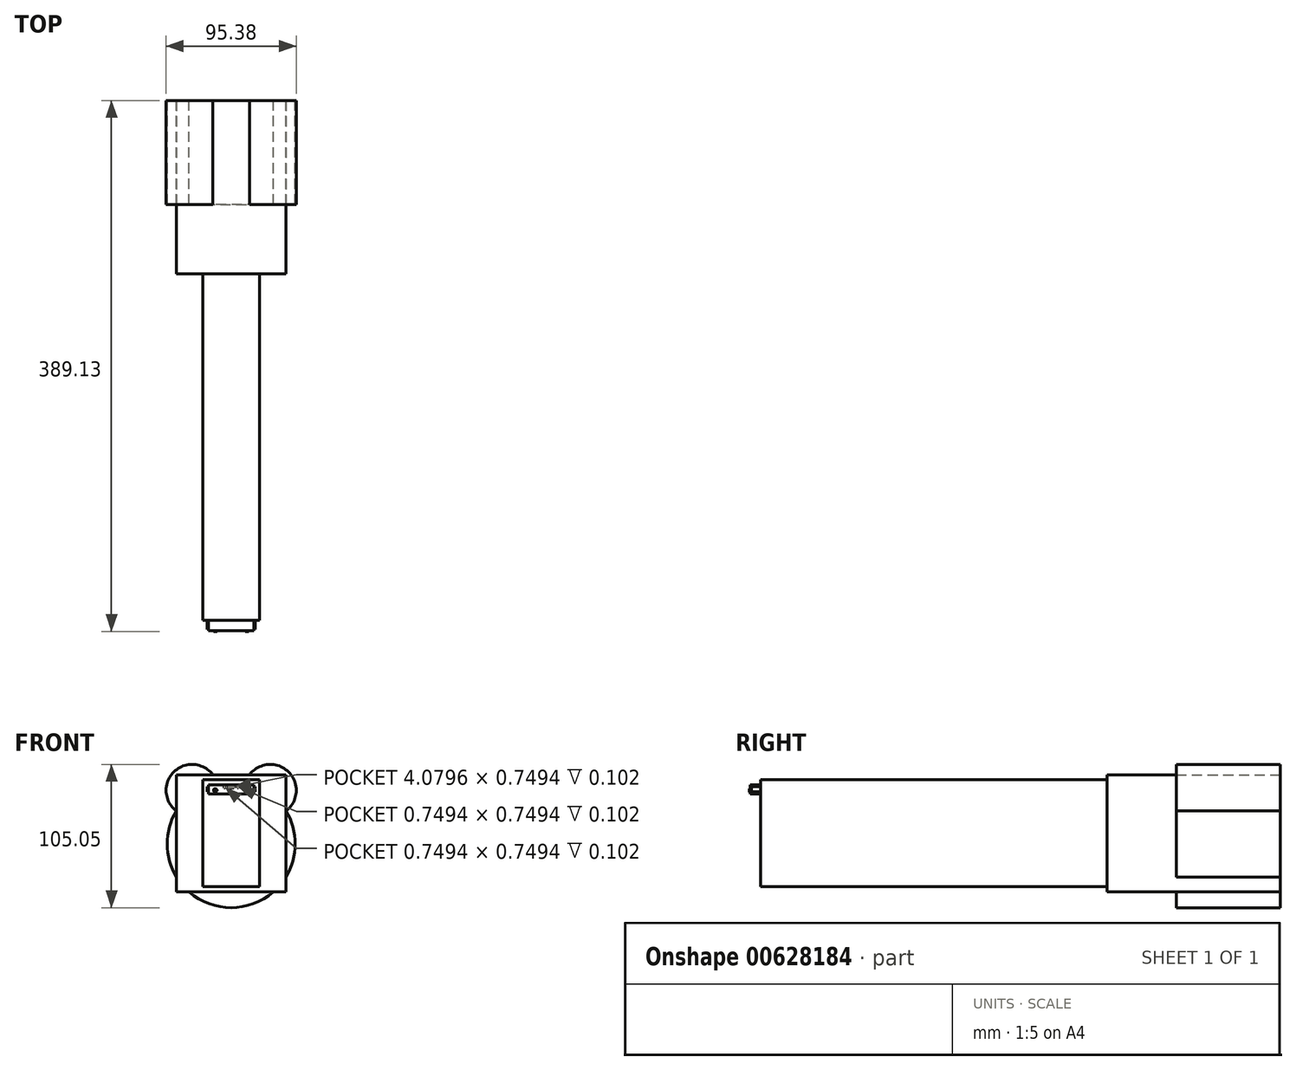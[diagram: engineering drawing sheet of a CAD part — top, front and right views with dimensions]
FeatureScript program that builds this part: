
annotation { "Feature Type Name" : "Feature", "Feature Type Description" : "" }
export const myFeature = defineFeature(function(context is Context, id is Id, definition is map)
    precondition{}
    {
        {
            var Q0;
            Q0=qCreatedBy(makeId("Front.planeOp"),FACE);
            var sketch = newSketch(context, id + "F0", { "sketchPlane" : qUnion([Q0])});
            skLineSegment(sketch, "E0.bottom", {"start": v(20.72, 39.2) * mm, "end": v(-20.72, 39.2) * mm});
            skLineSegment(sketch, "E0.top", {"start": v(20.72, -39.2) * mm, "end": v(-20.72, -39.2) * mm});
            skLineSegment(sketch, "E0.left", {"start": v(20.72, 39.2) * mm, "end": v(20.72, -39.2) * mm});
            skLineSegment(sketch, "E0.right", {"start": v(-20.72, 39.2) * mm, "end": v(-20.72, -39.2) * mm});
            skPoint(sketch, "E0.middle", {"position": v(0, 0) * mm});
            skSolve(sketch);
        }
        {
            var Q0;
            Q0 = qSketchRegion(id + "F0", true);
            extrude(context, id + "F1", {"entities" : qUnion([Q0]), "depth" : 254 * mm, "offsetDistance" : 25.4 * mm});
        }
        {
            var Q0;
            Q0=qCreatedBy(makeId("Front.planeOp"),FACE);
            var sketch = newSketch(context, id + "F2", { "sketchPlane" : qUnion([Q0])});
            skLineSegment(sketch, "E1.bottom", {"start": v(-40.07, 42.92) * mm, "end": v(40.07, 42.92) * mm});
            skLineSegment(sketch, "E1.top", {"start": v(-40.07, -42.92) * mm, "end": v(40.07, -42.92) * mm});
            skLineSegment(sketch, "E1.left", {"start": v(-40.07, 42.92) * mm, "end": v(-40.07, -42.92) * mm});
            skLineSegment(sketch, "E1.right", {"start": v(40.07, 42.92) * mm, "end": v(40.07, -42.92) * mm});
            skPoint(sketch, "E1.middle", {"position": v(0, 0) * mm});
            skSolve(sketch);
        }
        {
            var Q0;
            Q0=makeQuery(id+"F2.imprint","IMPRINT",FACE,{"disambiguationData":[TD([[makeQuery(id+"F2.imprint","IMPRINT",EDGE,{"derivedFrom":sQuery(id+"F2.wireOp",EDGE,"E1.bottom")}),-1.0]])]});
            extrude(context, id + "F3", {"entities" : qUnion([Q0]), "operationType" : NewBodyOperationType.ADD, "oppositeDirection" : true, "depth" : 127 * mm, "offsetDistance" : 25.4 * mm});
        }
        {
            var Q0;
            Q0=makeQuery(id+"F1.opExtrude","CAP_FACE",FACE,{"disambiguationData":[OSD([sQuery(id+"F0.wireOp",EDGE,"E0.bottom"),sQuery(id+"F0.wireOp",EDGE,"E0.top"),sQuery(id+"F0.wireOp",EDGE,"E0.left"),sQuery(id+"F0.wireOp",EDGE,"E0.right")])],"isStart":false});
            var sketch = newSketch(context, id + "F4", { "sketchPlane" : qUnion([Q0])});
            skLineSegment(sketch, "E2.bottom", {"start": v(16.75, 29.03) * mm, "end": v(-16.75, 29.03) * mm});
            skLineSegment(sketch, "E2.top", {"start": v(16.75, 35.48) * mm, "end": v(-16.75, 35.48) * mm});
            skLineSegment(sketch, "E2.left", {"start": v(16.75, 29.03) * mm, "end": v(16.75, 35.48) * mm});
            skLineSegment(sketch, "E2.right", {"start": v(-16.75, 29.03) * mm, "end": v(-16.75, 35.48) * mm});
            skPoint(sketch, "E2.middle", {"position": v(0, 32.25) * mm});
            skSolve(sketch);
        }
        {
            var Q0;
            Q0 = qSketchRegion(id + "F4", true);
            extrude(context, id + "F5", {"entities" : qUnion([Q0]), "operationType" : NewBodyOperationType.ADD, "depth" : 7.62 * mm, "offsetDistance" : 25.4 * mm});
        }
        {
            var Q0;
            Q0=makeQuery(id+"F5.opExtrude","CAP_FACE",FACE,{"disambiguationData":[OSD([sQuery(id+"F4.wireOp",EDGE,"E2.bottom"),sQuery(id+"F4.wireOp",EDGE,"E2.top"),sQuery(id+"F4.wireOp",EDGE,"E2.left"),sQuery(id+"F4.wireOp",EDGE,"E2.right")])],"isStart":false});
            var sketch = newSketch(context, id + "F6", { "sketchPlane" : qUnion([Q0])});
            skLineSegment(sketch, "E3.bottom", {"start": v(2.04, 33.46) * mm, "end": v(-2.04, 33.46) * mm});
            skLineSegment(sketch, "E3.top", {"start": v(2.04, 34.2) * mm, "end": v(-2.04, 34.2) * mm});
            skLineSegment(sketch, "E3.left", {"start": v(2.04, 33.46) * mm, "end": v(2.04, 34.2) * mm});
            skLineSegment(sketch, "E3.right", {"start": v(-2.04, 33.46) * mm, "end": v(-2.04, 34.2) * mm});
            skPoint(sketch, "E3.middle", {"position": v(0, 33.83) * mm});
            skLineSegment(sketch, "E4.bottom", {"start": v(4.58, 34.2) * mm, "end": v(5.33, 34.2) * mm});
            skLineSegment(sketch, "E4.top", {"start": v(4.58, 33.46) * mm, "end": v(5.33, 33.46) * mm});
            skLineSegment(sketch, "E4.left", {"start": v(4.58, 34.2) * mm, "end": v(4.58, 33.46) * mm});
            skLineSegment(sketch, "E4.right", {"start": v(5.33, 34.2) * mm, "end": v(5.33, 33.46) * mm});
            skLineSegment(sketch, "E5.bottom", {"start": v(-4.58, 34.2) * mm, "end": v(-5.33, 34.2) * mm});
            skLineSegment(sketch, "E5.top", {"start": v(-4.58, 33.46) * mm, "end": v(-5.33, 33.46) * mm});
            skLineSegment(sketch, "E5.left", {"start": v(-4.58, 34.2) * mm, "end": v(-4.58, 33.46) * mm});
            skLineSegment(sketch, "E5.right", {"start": v(-5.33, 34.2) * mm, "end": v(-5.33, 33.46) * mm});
            skSolve(sketch);
        }
        {
            var Q0;
            Q0 = qSketchRegion(id + "F6", true);
            extrude(context, id + "F7", {"entities" : qUnion([Q0]), "operationType" : NewBodyOperationType.REMOVE, "oppositeDirection" : true, "depth" : 0.1 * mm, "offsetDistance" : 25.4 * mm});
        }
        {
            var Q0;
            Q0=makeQuery(id+"F5.opExtrude","CAP_FACE",FACE,{"disambiguationData":[OSD([sQuery(id+"F4.wireOp",EDGE,"E2.bottom"),sQuery(id+"F4.wireOp",EDGE,"E2.top"),sQuery(id+"F4.wireOp",EDGE,"E2.left"),sQuery(id+"F4.wireOp",EDGE,"E2.right")])],"isStart":false});
            var sketch = newSketch(context, id + "F8", { "sketchPlane" : qUnion([Q0])});
            skCircle(sketch, "E6", {"center": v(-11.67, 31.57) * mm, "radius": 1.27 * mm});
            skCircle(sketch, "E7", {"center": v(11.67, 31.57) * mm, "radius": 1.27 * mm});
            skSolve(sketch);
        }
        {
            var Q0;
            Q0 = qSketchRegion(id + "F8", true);
            extrude(context, id + "F9", {"entities" : qUnion([Q0]), "operationType" : NewBodyOperationType.ADD, "depth" : 0.5 * mm, "offsetDistance" : 25.4 * mm});
        }
        {
            var Q0;
            Q0=makeQuery(id+"F1.opExtrude","CAP_FACE",FACE,{"disambiguationData":[OSD([sQuery(id+"F0.wireOp",EDGE,"E0.bottom"),sQuery(id+"F0.wireOp",EDGE,"E0.top"),sQuery(id+"F0.wireOp",EDGE,"E0.left"),sQuery(id+"F0.wireOp",EDGE,"E0.right")])],"isStart":false});
            var sketch = newSketch(context, id + "F10", { "sketchPlane" : qUnion([Q0])});
            skLineSegment(sketch, "E8.bottom", {"start": v(-16.75, 34.2) * mm, "end": v(-17.5, 34.2) * mm});
            skLineSegment(sketch, "E8.top", {"start": v(-16.75, 30.4) * mm, "end": v(-17.5, 30.4) * mm});
            skLineSegment(sketch, "E8.left", {"start": v(-16.75, 34.2) * mm, "end": v(-16.75, 30.4) * mm});
            skLineSegment(sketch, "E8.right", {"start": v(-17.5, 34.2) * mm, "end": v(-17.5, 30.4) * mm});
            skLineSegment(sketch, "E9.bottom", {"start": v(16.75, 34.2) * mm, "end": v(17.5, 34.2) * mm});
            skLineSegment(sketch, "E9.top", {"start": v(16.75, 30.4) * mm, "end": v(17.5, 30.4) * mm});
            skLineSegment(sketch, "E9.left", {"start": v(16.75, 34.2) * mm, "end": v(16.75, 30.4) * mm});
            skLineSegment(sketch, "E9.right", {"start": v(17.5, 34.2) * mm, "end": v(17.5, 30.4) * mm});
            skSolve(sketch);
        }
        {
            var Q0;
            Q0 = qSketchRegion(id + "F10", true);
            extrude(context, id + "F11", {"entities" : qUnion([Q0]), "operationType" : NewBodyOperationType.ADD, "depth" : 6.6 * mm, "offsetDistance" : 25.4 * mm});
        }
        {
            var Q0;
            Q0=makeQuery(id+"F3.opExtrude","CAP_FACE",FACE,{"disambiguationData":[OSD([sQuery(id+"F2.wireOp",EDGE,"E1.bottom"),sQuery(id+"F2.wireOp",EDGE,"E1.top"),sQuery(id+"F2.wireOp",EDGE,"E1.left"),sQuery(id+"F2.wireOp",EDGE,"E1.right")])],"isStart":false});
            var sketch = newSketch(context, id + "F12", { "sketchPlane" : qUnion([Q0])});
            skCircle(sketch, "E10", {"center": v(-28.64, 31.5) * mm, "radius": 19.05 * mm});
            skCircle(sketch, "E11", {"center": v(28.64, 31.5) * mm, "radius": 19.05 * mm});
            skCircle(sketch, "E12", {"center": v(0, -7.62) * mm, "radius": 46.89 * mm});
            skSolve(sketch);
        }
        {
            var Q0;
            Q0 = qSketchRegion(id + "F12", true);
            extrude(context, id + "F13", {"entities" : qUnion([Q0]), "operationType" : NewBodyOperationType.ADD, "oppositeDirection" : true, "depth" : 76.2 * mm, "offsetDistance" : 25.4 * mm});
        }
    });
